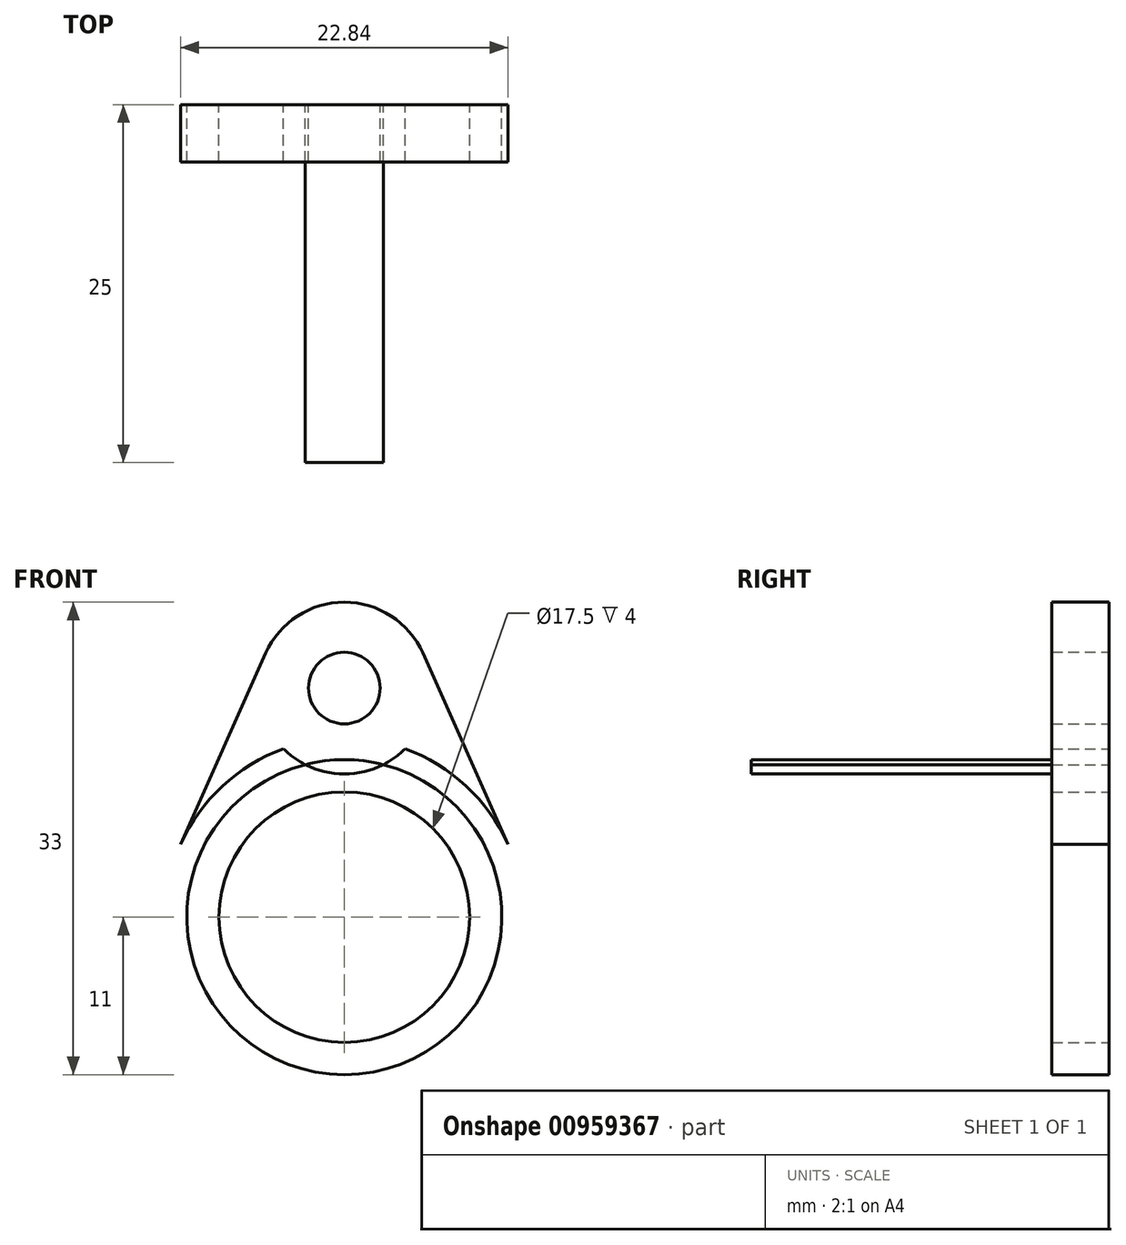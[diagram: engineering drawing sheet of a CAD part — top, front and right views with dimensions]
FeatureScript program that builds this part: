
annotation { "Feature Type Name" : "Feature", "Feature Type Description" : "" }
export const myFeature = defineFeature(function(context is Context, id is Id, definition is map)
    precondition{}
    {
        {
            var Q0;
            Q0=qCreatedBy(makeId("Front.planeOp"),FACE);
            var sketch = newSketch(context, id + "F0", { "sketchPlane" : qUnion([Q0])});
            skCircle(sketch, "E0", {"center": v(0, 0) * mm, "radius": 11 * mm});
            skCircle(sketch, "E1", {"center": v(0, 0) * mm, "radius": 12.5 * mm});
            skCircle(sketch, "E2", {"center": v(0, 16) * mm, "radius": 2.5 * mm});
            skCircle(sketch, "E3", {"center": v(0, 16) * mm, "radius": 6 * mm});
            skLineSegment(sketch, "E4", {"start": v(-5.48, 18.44) * mm, "end": v(-11.42, 5.08) * mm});
            skLineSegment(sketch, "E5", {"start": v(5.48, 18.44) * mm, "end": v(11.42, 5.08) * mm});
            skCircle(sketch, "E6", {"center": v(0, 0) * mm, "radius": 8.75 * mm});
            skSolve(sketch);
        }
        {
            var Q0;
            {var subQ0=sQuery(id+"F0.wireOp",EDGE,"E4");Q0=makeQuery(id+"F0.imprint","IMPRINT",FACE,{"disambiguationData":[TD([[makeQuery(id+"F0.imprint","IMPRINT",EDGE,{"derivedFrom":subQ0}),1.0]])]});}
            var Q1;
            {var subQ0=sQuery(id+"F0.wireOp",EDGE,"E5");Q1=makeQuery(id+"F0.imprint","IMPRINT",FACE,{"disambiguationData":[TD([[makeQuery(id+"F0.imprint","IMPRINT",EDGE,{"derivedFrom":subQ0}),-1.0]])]});}
            var Q2;
            Q2=makeQuery(id+"F0.imprint","IMPRINT",FACE,{"disambiguationData":[TD([[makeQuery(id+"F0.imprint","IMPRINT",EDGE,{"derivedFrom":sQuery(id+"F0.wireOp",EDGE,"E2")}),-1.0]])]});
            var Q3;
            Q3=makeQuery(id+"F0.imprint","IMPRINT",FACE,{"disambiguationData":[TD([[makeQuery(id+"F0.imprint","IMPRINT",EDGE,{"derivedFrom":sQuery(id+"F0.wireOp",EDGE,"E0")}),-1.0]])]});
            var Q4;
            {var subQ3=sQuery(id+"F0.wireOp",EDGE,"E3");var subQ6=sQuery(id+"F0.wireOp",EDGE,"E0");var subQ7=makeQuery(id+"F0.imprint","INTERSECT",VERTEX,{"disambiguationData":[OD(0.0)],"derivedFrom":[subQ6,subQ3]});Q4=makeQuery(id+"F0.imprint","IMPRINT",FACE,{"disambiguationData":[TD([[makeQuery(id+"F0.imprint","IMPRINT",EDGE,{"disambiguationData":[TD([[subQ7,-1.0]])],"derivedFrom":subQ6}),-1.0]])]});}
            var Q5;
            {var subQ0=sQuery(id+"F0.wireOp",EDGE,"E3");var subQ1=sQuery(id+"F0.wireOp",EDGE,"E0");var subQ2=makeQuery(id+"F0.imprint","INTERSECT",VERTEX,{"disambiguationData":[OD(0.0)],"derivedFrom":[subQ1,subQ0]});Q5=makeQuery(id+"F0.imprint","IMPRINT",FACE,{"disambiguationData":[TD([[makeQuery(id+"F0.imprint","IMPRINT",EDGE,{"disambiguationData":[TD([[subQ2,-1.0]])],"derivedFrom":subQ1}),1.0]])]});}
            var Q6;
            {var subQ0=sQuery(id+"F0.wireOp",EDGE,"E3");var subQ1=sQuery(id+"F0.wireOp",EDGE,"E0");var subQ2=makeQuery(id+"F0.imprint","INTERSECT",VERTEX,{"disambiguationData":[OD(0.0)],"derivedFrom":[subQ1,subQ0]});Q6=makeQuery(id+"F0.imprint","IMPRINT",FACE,{"disambiguationData":[TD([[makeQuery(id+"F0.imprint","IMPRINT",EDGE,{"disambiguationData":[TD([[subQ2,1.0]])],"derivedFrom":subQ1}),1.0]])]});}
            extrude(context, id + "F1", {"entities" : qUnion([Q0, Q1, Q2, Q3, Q4, Q5, Q6]), "depth" : 4 * mm, "offsetDistance" : 25 * mm});
        }
        {
            var Q0;
            {var subQ0=sQuery(id+"F0.wireOp",EDGE,"E3");var subQ1=sQuery(id+"F0.wireOp",EDGE,"E0");var subQ2=makeQuery(id+"F0.imprint","INTERSECT",VERTEX,{"disambiguationData":[OD(0.0)],"derivedFrom":[subQ1,subQ0]});Q0=makeQuery(id+"F0.imprint","IMPRINT",FACE,{"disambiguationData":[TD([[makeQuery(id+"F0.imprint","IMPRINT",EDGE,{"disambiguationData":[TD([[subQ2,-1.0]])],"derivedFrom":subQ1}),1.0]])]});}
            extrude(context, id + "F2", {"entities" : qUnion([Q0]), "operationType" : NewBodyOperationType.ADD, "depth" : 25 * mm, "offsetDistance" : 25 * mm});
        }
    });
